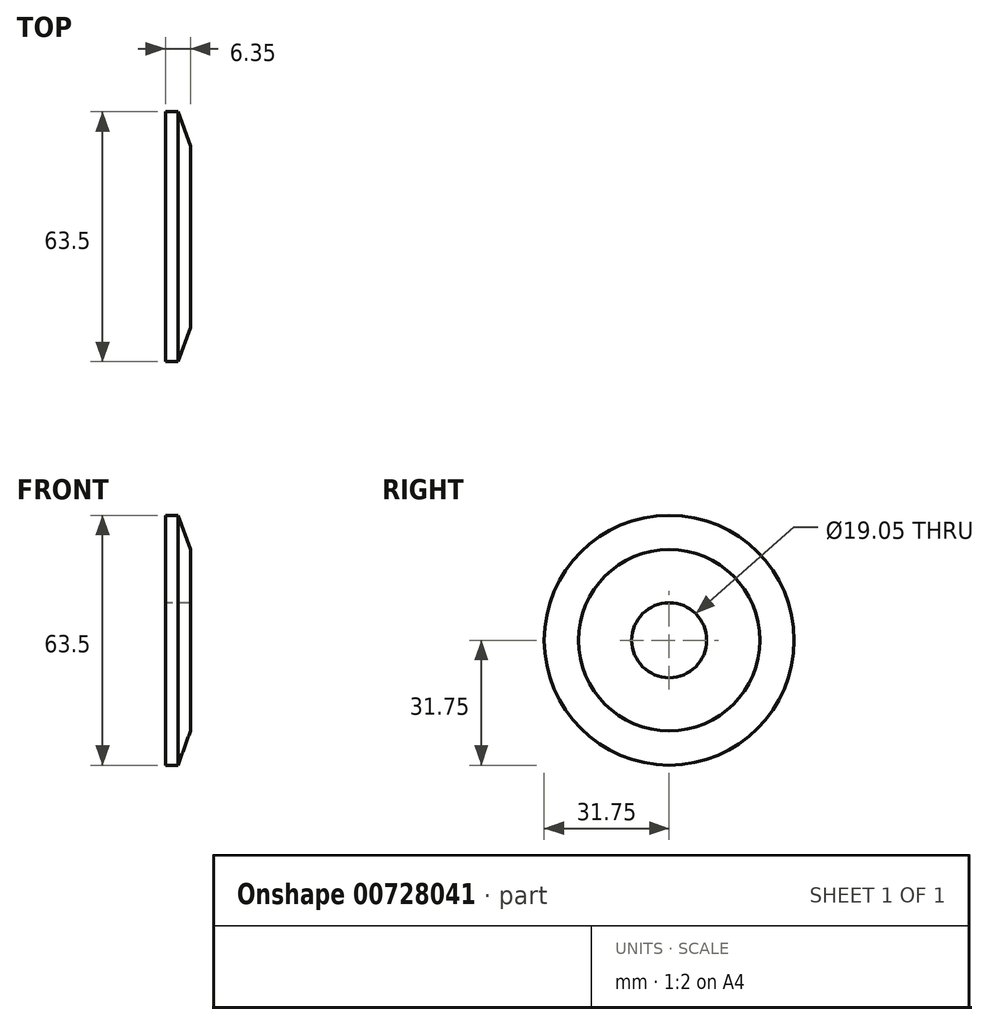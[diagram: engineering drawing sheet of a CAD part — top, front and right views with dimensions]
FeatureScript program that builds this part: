
annotation { "Feature Type Name" : "Feature", "Feature Type Description" : "" }
export const myFeature = defineFeature(function(context is Context, id is Id, definition is map)
    precondition{}
    {
        {
            var Q0;
            Q0=qCreatedBy(makeId("Front.planeOp"),FACE);
            var sketch = newSketch(context, id + "F0", { "sketchPlane" : qUnion([Q0])});
            skLineSegment(sketch, "E0", {"start": v(0, 0) * mm, "end": v(0, 31.75) * mm});
            skLineSegment(sketch, "E1", {"start": v(0, 31.75) * mm, "end": v(3.17, 31.75) * mm});
            skLineSegment(sketch, "E2", {"start": v(3.17, 31.75) * mm, "end": v(6.35, 23.03) * mm});
            skLineSegment(sketch, "E3", {"start": v(6.35, 23.03) * mm, "end": v(6.35, 0) * mm});
            skLineSegment(sketch, "E4", {"start": v(6.35, 0) * mm, "end": v(0, 0) * mm});
            skSolve(sketch);
        }
        {
            var Q0;
            Q0=makeQuery(id+"F0.imprint","IMPRINT",FACE,{"disambiguationData":[TD([[makeQuery(id+"F0.imprint","IMPRINT",EDGE,{"derivedFrom":sQuery(id+"F0.wireOp",EDGE,"E0")}),-1.0]])]});
            var Q1;
            Q1=sQuery(id+"F0.wireOp",EDGE,"E4");
            revolve(context, id + "F1", {"surfaceOperationType" : NewSurfaceOperationType.NEW, "entities" : qUnion([Q0]), "axis" : qUnion([Q1]), "revolveType" : RevolveType.FULL});
        }
        {
            var Q0;
            Q0=makeQuery(id+"F1.opRevolve","SWEPT_FACE",FACE,{"disambiguationData":[OSD([sQuery(id+"F0.wireOp",EDGE,"E0")])]});
            var sketch = newSketch(context, id + "F2", { "sketchPlane" : qUnion([Q0])});
            skCircle(sketch, "E5", {"center": v(0, 0) * mm, "radius": 9.53 * mm});
            skSolve(sketch);
        }
        {
            var Q0;
            Q0=makeQuery(id+"F2.imprint","IMPRINT",FACE,{"disambiguationData":[TD([[makeQuery(id+"F2.imprint","IMPRINT",EDGE,{"derivedFrom":sQuery(id+"F2.wireOp",EDGE,"E5")}),1.0]])]});
            extrude(context, id + "F3", {"entities" : qUnion([Q0]), "operationType" : NewBodyOperationType.REMOVE, "endBound" : BoundingType.THROUGH_ALL, "oppositeDirection" : true, "depth" : 25.4 * mm, "offsetDistance" : 25.4 * mm});
        }
    });
